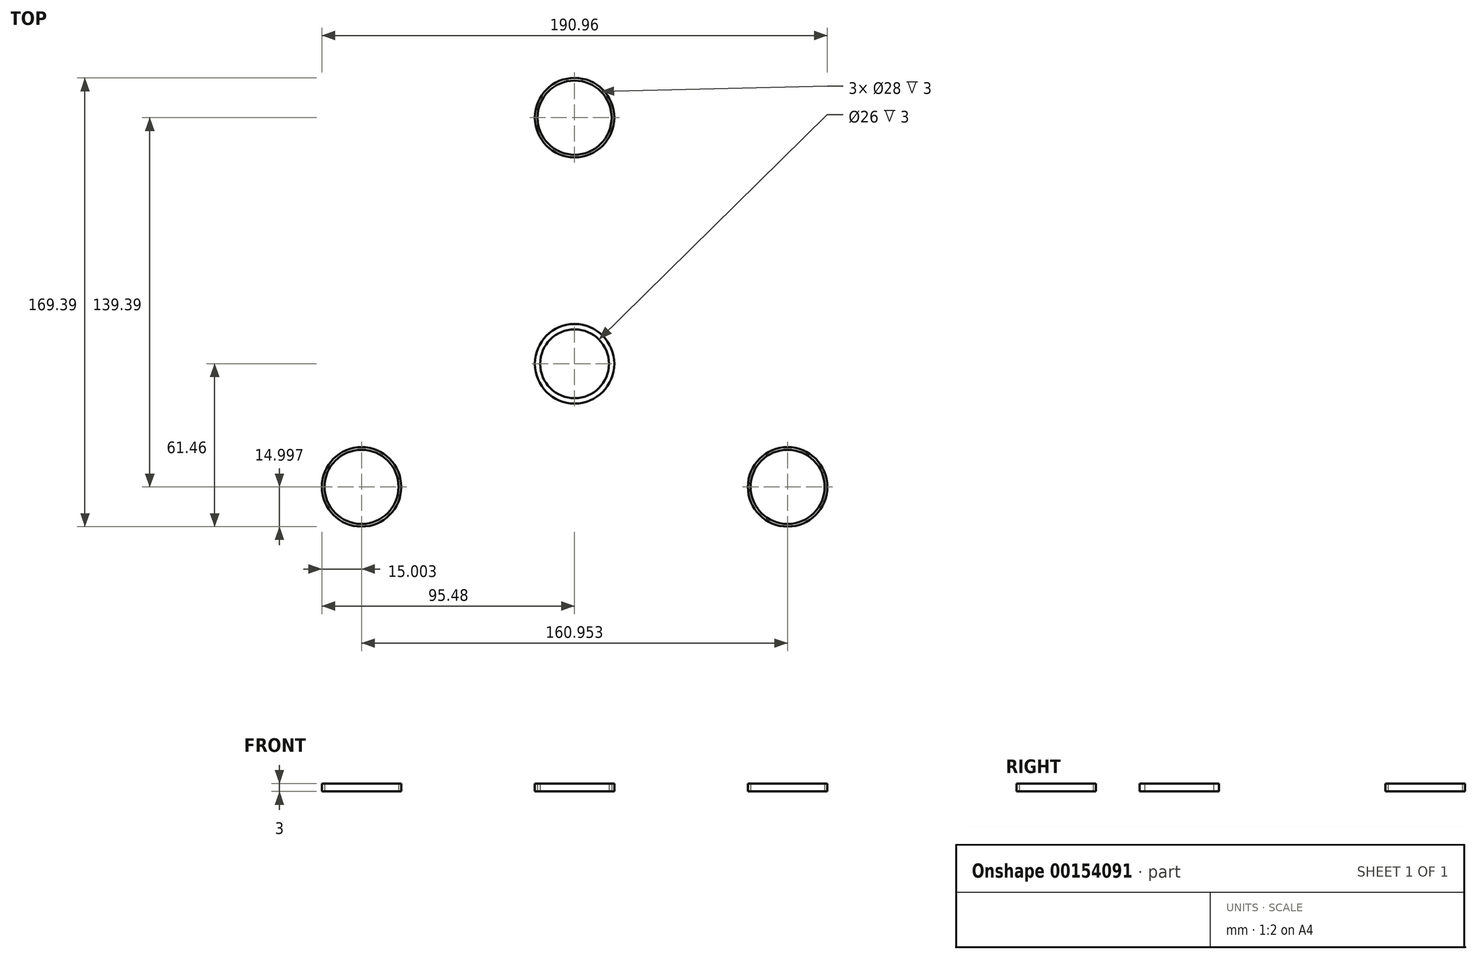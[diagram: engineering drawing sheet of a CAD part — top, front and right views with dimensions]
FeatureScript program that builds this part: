
annotation { "Feature Type Name" : "Feature", "Feature Type Description" : "" }
export const myFeature = defineFeature(function(context is Context, id is Id, definition is map)
    precondition{}
    {
        {
            var Q0;
            Q0=qCreatedBy(makeId("Top.planeOp"),FACE);
            var sketch = newSketch(context, id + "F0", { "sketchPlane" : qUnion([Q0])});
            skCircle(sketch, "E0", {"center": v(0, 0) * mm, "radius": 125 * mm, "construction": true});
            skLineSegment(sketch, "E1", {"start": v(0, 0) * mm, "end": v(0, 125) * mm, "construction": true});
            skLineSegment(sketch, "E2", {"start": v(0, 0) * mm, "end": v(108.25, -62.5) * mm, "construction": true});
            skLineSegment(sketch, "E3", {"start": v(0, 0) * mm, "end": v(-108.25, -62.5) * mm, "construction": true});
            skCircle(sketch, "E4", {"center": v(0, 0) * mm, "radius": 92.93 * mm, "construction": true});
            skCircle(sketch, "E5", {"center": v(0, 92.93) * mm, "radius": 15 * mm});
            skCircle(sketch, "E6", {"center": v(80.48, -46.46) * mm, "radius": 15 * mm});
            skCircle(sketch, "E7", {"center": v(0, 0) * mm, "radius": 15 * mm});
            skCircle(sketch, "E8", {"center": v(-80.48, -46.46) * mm, "radius": 15 * mm});
            skCircle(sketch, "E9", {"center": v(0, 92.93) * mm, "radius": 14 * mm});
            skCircle(sketch, "E10", {"center": v(80.48, -46.46) * mm, "radius": 14 * mm});
            skCircle(sketch, "E11", {"center": v(0, 0) * mm, "radius": 13 * mm});
            skCircle(sketch, "E12", {"center": v(-80.48, -46.46) * mm, "radius": 14 * mm});
            skSolve(sketch);
        }
        {
            var Q0;
            Q0=makeQuery(id+"F0.imprint","IMPRINT",FACE,{"disambiguationData":[TD([[makeQuery(id+"F0.imprint","IMPRINT",EDGE,{"derivedFrom":sQuery(id+"F0.wireOp",EDGE,"e663e824-24ac-43a2-836d-71c5ef75fede.sketch_text.stroke-0")}),1.0]])]});
            var Q1;
            Q1=makeQuery(id+"F0.imprint","IMPRINT",FACE,{"disambiguationData":[TD([[makeQuery(id+"F0.imprint","IMPRINT",EDGE,{"derivedFrom":sQuery(id+"F0.wireOp",EDGE,"37f9b0bd-fe51-47b8-a9f5-edb700452e8e.1.0")}),1.0]])]});
            var Q2;
            Q2=makeQuery(id+"F0.imprint","IMPRINT",FACE,{"disambiguationData":[TD([[makeQuery(id+"F0.imprint","IMPRINT",EDGE,{"derivedFrom":sQuery(id+"F0.wireOp",EDGE,"yCQaDQJ6-h36W-EIj1-Q2Cl-sdCPvGYDcxaW.bottom")}),1.0]])]});
            var Q3;
            Q3=makeQuery(id+"F0.imprint","IMPRINT",FACE,{"disambiguationData":[TD([[makeQuery(id+"F0.imprint","IMPRINT",EDGE,{"derivedFrom":sQuery(id+"F0.wireOp",EDGE,"w6QDhoMs-LHrf-8Ccj-0OIK-4ClMXiJJT541.bottom")}),-1.0]])]});
            var Q4;
            Q4=makeQuery(id+"F0.imprint","IMPRINT",FACE,{"disambiguationData":[TD([[makeQuery(id+"F0.imprint","IMPRINT",EDGE,{"derivedFrom":sQuery(id+"F0.wireOp",EDGE,"37f9b0bd-fe51-47b8-a9f5-edb700452e8e.2.0")}),1.0]])]});
            var Q5;
            Q5=makeQuery(id+"F0.imprint","IMPRINT",FACE,{"disambiguationData":[TD([[makeQuery(id+"F0.imprint","IMPRINT",EDGE,{"derivedFrom":sQuery(id+"F0.wireOp",EDGE,"588eb70c-c697-4d0d-8be9-4c09f1b8cc37.sketch_text.stroke-0")}),1.0]])]});
            var Q6;
            Q6=makeQuery(id+"F0.imprint","IMPRINT",FACE,{"disambiguationData":[TD([[makeQuery(id+"F0.imprint","IMPRINT",EDGE,{"derivedFrom":sQuery(id+"F0.wireOp",EDGE,"9a9fce55-55e2-4091-9942-b0ef39464490.sketch_text.stroke-0")}),-1.0]])]});
            var Q7;
            Q7=qSketchRegion(id+"F0",true);
            var Q8;
            Q8=makeQuery(id+"F0.imprint","IMPRINT",FACE,{"disambiguationData":[TD([[makeQuery(id+"F0.imprint","IMPRINT",EDGE,{"derivedFrom":sQuery(id+"F0.wireOp",EDGE,"a675f789-81a3-41d5-a266-0becbd7d80d0.sketch_text.stroke-0")}),1.0]])]});
            extrude(context, id + "F1", {"entities" : qUnion([Q0, Q1, Q2, Q3, Q4, Q5, Q6, Q7, Q8]), "offsetDistance" : 25 * mm, "depth" : 3 * mm});
        }
    });
